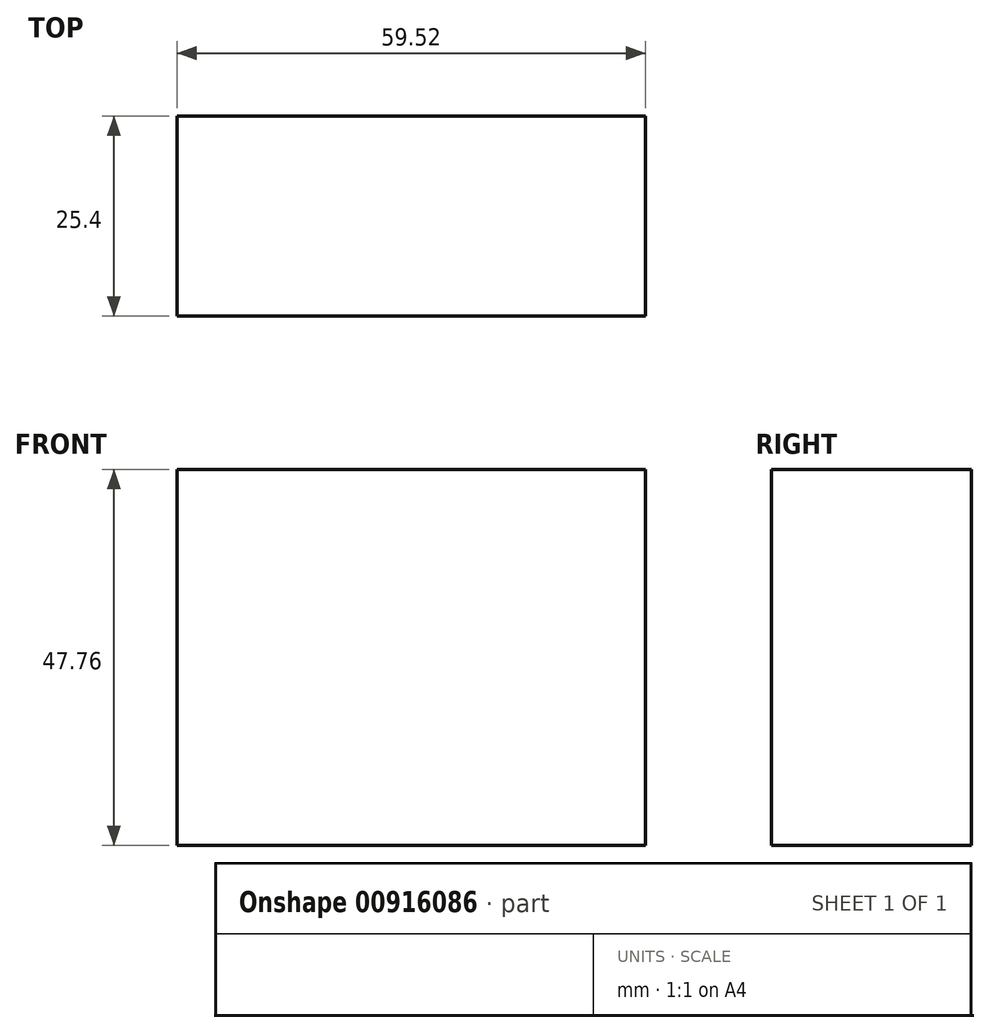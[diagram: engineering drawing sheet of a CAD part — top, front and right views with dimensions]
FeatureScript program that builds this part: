
annotation { "Feature Type Name" : "Feature", "Feature Type Description" : "" }
export const myFeature = defineFeature(function(context is Context, id is Id, definition is map)
    precondition{}
    {
        {
            var Q0;
            Q0=qCreatedBy(makeId("Front.planeOp"),FACE);
            var sketch = newSketch(context, id + "F0", { "sketchPlane" : qUnion([Q0])});
            skLineSegment(sketch, "E0.bottom", {"start": v(-59.52, 47.76) * mm, "end": v(0, 47.76) * mm});
            skLineSegment(sketch, "E0.top", {"start": v(-59.52, 0) * mm, "end": v(0, 0) * mm});
            skLineSegment(sketch, "E0.left", {"start": v(-59.52, 47.76) * mm, "end": v(-59.52, 0) * mm});
            skLineSegment(sketch, "E0.right", {"start": v(0, 47.76) * mm, "end": v(0, 0) * mm});
            skSolve(sketch);
        }
        {
            var Q0;
            Q0 = qSketchRegion(id + "F0", true);
            extrude(context, id + "F1", {"entities" : qUnion([Q0]), "depth" : 25.4 * mm, "offsetDistance" : 25.4 * mm});
        }
    });
